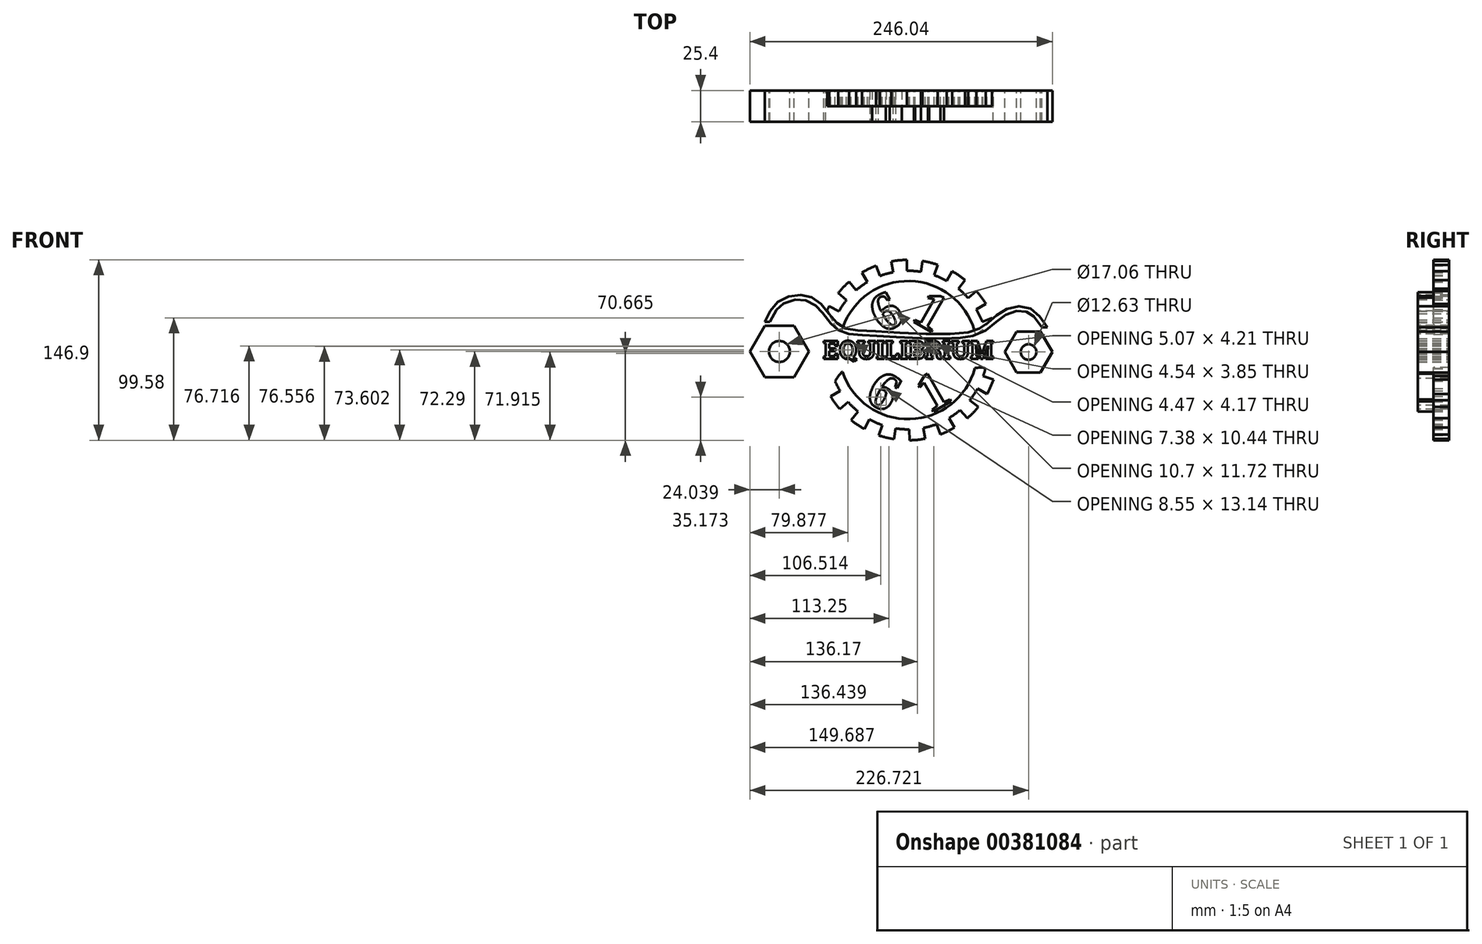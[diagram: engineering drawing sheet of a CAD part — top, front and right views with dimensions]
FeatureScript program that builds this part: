
annotation { "Feature Type Name" : "Feature", "Feature Type Description" : "" }
export const myFeature = defineFeature(function(context is Context, id is Id, definition is map)
    precondition{}
    {
        {
            var Q0;
            Q0=qCreatedBy(makeId("Front.planeOp"),FACE);
            var sketch = newSketch(context, id + "F0", { "sketchPlane" : qUnion([Q0])});
            skCircle(sketch, "E0.cCircle", {"center": v(93.86, 118.06) * mm, "radius": 16.73 * mm, "construction": true});
            skLineSegment(sketch, "E0.0", {"start": v(74.54, 118.06) * mm, "end": v(84.2, 134.79) * mm});
            skLineSegment(sketch, "E0.1", {"start": v(84.2, 134.79) * mm, "end": v(103.52, 134.79) * mm});
            skLineSegment(sketch, "E0.2", {"start": v(103.52, 134.79) * mm, "end": v(113.18, 118.06) * mm});
            skLineSegment(sketch, "E0.3", {"start": v(113.18, 118.06) * mm, "end": v(103.52, 101.32) * mm});
            skLineSegment(sketch, "E0.4", {"start": v(103.52, 101.32) * mm, "end": v(84.2, 101.32) * mm});
            skLineSegment(sketch, "E0.5", {"start": v(84.2, 101.32) * mm, "end": v(74.54, 118.06) * mm});
            skPoint(sketch, "E0.0.midPoint", {"position": v(79.37, 126.42) * mm});
            skCircle(sketch, "E1.cCircle", {"center": v(-108.82, 118.43) * mm, "radius": 20.82 * mm, "construction": true});
            skLineSegment(sketch, "E1.0", {"start": v(-84.78, 118.43) * mm, "end": v(-96.8, 97.61) * mm});
            skLineSegment(sketch, "E1.1", {"start": v(-96.8, 97.61) * mm, "end": v(-120.84, 97.61) * mm});
            skLineSegment(sketch, "E1.2", {"start": v(-120.84, 97.61) * mm, "end": v(-132.86, 118.43) * mm});
            skLineSegment(sketch, "E1.3", {"start": v(-132.86, 118.43) * mm, "end": v(-120.84, 139.25) * mm});
            skLineSegment(sketch, "E1.4", {"start": v(-120.84, 139.25) * mm, "end": v(-96.8, 139.25) * mm});
            skLineSegment(sketch, "E1.5", {"start": v(-96.8, 139.25) * mm, "end": v(-84.78, 118.43) * mm});
            skPoint(sketch, "E1.0.midPoint", {"position": v(-90.8, 108.02) * mm});
            skCircle(sketch, "E2", {"center": v(-108.82, 118.43) * mm, "radius": 8.53 * mm});
            skCircle(sketch, "E3", {"center": v(93.86, 118.06) * mm, "radius": 6.32 * mm});
            skLineSegment(sketch, "E4.0", {"start": v(82.3, 138.1) * mm, "end": v(109.3, 138.1) * mm});
            skLineSegment(sketch, "E4.1", {"start": v(70.73, 118.06) * mm, "end": v(82.3, 138.1) * mm});
            skLineSegment(sketch, "E4.2", {"start": v(82.3, 98.02) * mm, "end": v(70.73, 118.06) * mm});
            skLineSegment(sketch, "E4.3", {"start": v(103.52, 98.02) * mm, "end": v(82.3, 98.02) * mm});
            skLineSegment(sketch, "E5.0", {"start": v(-94.9, 94.3) * mm, "end": v(-120.84, 94.3) * mm});
            skLineSegment(sketch, "E5.1", {"start": v(-80.97, 118.43) * mm, "end": v(-94.9, 94.3) * mm});
            skLineSegment(sketch, "E5.2", {"start": v(-94.9, 142.55) * mm, "end": v(-80.97, 118.43) * mm});
            skLineSegment(sketch, "E5.3", {"start": v(-120.84, 142.55) * mm, "end": v(-94.9, 142.55) * mm});
            skFitSpline(sketch, "E6", {"points": [v(-120.84, 142.55) * mm, v(-109.54, 159.3) * mm, v(-89.24, 164.37) * mm, v(-74.01, 156.03) * mm, v(-59.88, 139.72) * mm, v(-39.18, 135.4) * mm, v(39.48, 133.4) * mm, v(59.02, 140.4) * mm, v(73.53, 151.68) * mm, v(93.84, 154.22) * mm, v(109.43, 137.9) * mm], "startDerivative": vector(96.51, 208.9) * mm, "endDerivative": vector(140.04, -213.02) * mm});
            skFitSpline(sketch, "E7", {"points": [v(-120.84, 94.3) * mm, v(-105.3, 79.6) * mm, v(-87.85, 76.94) * mm, v(-69.52, 87.59) * mm, v(-57.71, 99.33) * mm, v(-35.67, 104.84) * mm, v(44.99, 104.34) * mm, v(59.43, 101.49) * mm, v(73.33, 88.48) * mm, v(88.11, 84.93) * mm, v(100.24, 90.84) * mm, v(103.52, 98.02) * mm], "startDerivative": vector(157.46, -185.5) * mm, "endDerivative": vector(35.32, 133.18) * mm});
            skLineSegment(sketch, "E8.2", {"start": v(-91.96, 145.1) * mm, "end": v(-77.3, 119.7) * mm});
            skLineSegment(sketch, "E8.3", {"start": v(-77.3, 117.16) * mm, "end": v(-91.96, 91.77) * mm});
            skLineSegment(sketch, "E8.4", {"start": v(-94.16, 90.5) * mm, "end": v(-106.94, 90.5) * mm});
            skLineSegment(sketch, "E9.0", {"start": v(81.56, 141.9) * mm, "end": v(96.75, 141.9) * mm});
            skLineSegment(sketch, "E9.1", {"start": v(67.06, 119.33) * mm, "end": v(79.36, 140.63) * mm});
            skLineSegment(sketch, "E9.2", {"start": v(79.36, 95.48) * mm, "end": v(67.06, 116.79) * mm});
            skFitSpline(sketch, "E10.trimOffspring", {"points": [v(-117.38, 140.95) * mm, v(-116.38, 143.13) * mm, v(-114.9, 146.3) * mm, v(-112.76, 150.07) * mm, v(-111.3, 152.18) * mm, v(-110.04, 153.7) * mm, v(-109.04, 154.74) * mm, v(-107.98, 155.7) * mm, v(-106.85, 156.56) * mm, v(-105.6, 157.36) * mm, v(-103.8, 158.33) * mm, v(-101.36, 159.35) * mm, v(-98.2, 160.21) * mm, v(-94.98, 160.7) * mm, v(-92.36, 160.8) * mm, v(-90.37, 160.68) * mm, v(-88.96, 160.5) * mm, v(-87.6, 160.22) * mm, v(-85.89, 159.75) * mm, v(-83.86, 158.93) * mm, v(-81.54, 157.6) * mm, v(-79.66, 156.17) * mm, v(-78.17, 154.83) * mm, v(-77.07, 153.73) * mm, v(-75.96, 152.52) * mm, v(-74.84, 151.2) * mm, v(-73.71, 149.82) * mm, v(-72.2, 147.88) * mm, v(-70.27, 145.36) * mm, v(-67.9, 142.34) * mm, v(-65.8, 139.95) * mm, v(-64, 138.2) * mm, v(-62.83, 137.17) * mm, v(-61.83, 136.42) * mm, v(-60.82, 135.71) * mm, v(-59.51, 134.94) * mm, v(-57.88, 134.17) * mm, v(-55.63, 133.34) * mm, v(-52.7, 132.64) * mm, v(-48.93, 132.16) * mm, v(-45.44, 131.92) * mm, v(-42.35, 131.75) * mm, v(-39.86, 131.62) * mm, v(-37.16, 131.47) * mm, v(-33.3, 131.25) * mm, v(-28, 130.93) * mm, v(-21.08, 130.52) * mm, v(-13.73, 130.1) * mm, v(-3.57, 129.58) * mm, v(6.83, 129.15) * mm, v(16.86, 128.92) * mm, v(24.05, 128.88) * mm, v(30.77, 129) * mm, v(35.86, 129.25) * mm, v(39.58, 129.56) * mm, v(42.16, 129.85) * mm, v(44.55, 130.21) * mm, v(47.52, 130.78) * mm, v(50.84, 131.65) * mm, v(54.34, 133) * mm, v(57.44, 134.62) * mm, v(60.2, 136.47) * mm, v(62.77, 138.52) * mm, v(65.22, 140.66) * mm, v(67.64, 142.8) * mm, v(70.09, 144.84) * mm, v(72.2, 146.41) * mm, v(73.96, 147.55) * mm, v(75.32, 148.33) * mm, v(76.75, 149.05) * mm, v(78.73, 149.91) * mm, v(81.32, 150.78) * mm, v(84.47, 151.43) * mm, v(87.01, 151.6) * mm, v(88.94, 151.5) * mm, v(90.31, 151.3) * mm, v(91.4, 151.03) * mm, v(92.21, 150.76) * mm, v(93, 150.45) * mm, v(93.98, 149.97) * mm, v(95.13, 149.25) * mm, v(96.28, 148.4) * mm, v(97.8, 147.05) * mm, v(99.68, 145.06) * mm, v(101.9, 142.24) * mm, v(104.07, 139.12) * mm, v(105.51, 136.92) * mm, v(106.24, 135.81) * mm]});
            skLineSegment(sketch, "E11.trimOffspring", {"start": v(-110.44, 146.36) * mm, "end": v(-94.16, 146.36) * mm});
            skLineSegment(sketch, "E12.trimOffspring", {"start": v(90.91, 94.21) * mm, "end": v(81.56, 94.21) * mm});
            skFitSpline(sketch, "E13.0", {"points": [v(-118.32, 96.45) * mm, v(-116.68, 94.52) * mm, v(-114.27, 91.67) * mm, v(-111.02, 88.26) * mm, v(-108.57, 85.95) * mm, v(-106.49, 84.29) * mm, v(-104.8, 83.14) * mm, v(-103.52, 82.37) * mm, v(-102.22, 81.7) * mm, v(-100.44, 80.93) * mm, v(-97.24, 79.9) * mm, v(-93.44, 79.5) * mm, v(-90.04, 79.85) * mm, v(-88.1, 80.26) * mm, v(-86.12, 80.82) * mm, v(-83.62, 81.79) * mm, v(-80.63, 83.32) * mm, v(-77.72, 85.15) * mm, v(-74.94, 87.2) * mm, v(-72.78, 89.05) * mm, v(-71.17, 90.56) * mm, v(-69.63, 92.11) * mm, v(-67.77, 94.1) * mm, v(-65.6, 96.5) * mm, v(-63.37, 98.83) * mm, v(-61.38, 100.67) * mm, v(-59.64, 102.03) * mm, v(-57.8, 103.28) * mm, v(-55.34, 104.61) * mm, v(-52.03, 105.85) * mm, v(-48.33, 106.78) * mm, v(-44.13, 107.45) * mm, v(-40.1, 107.85) * mm, v(-36.5, 108.1) * mm, v(-33.59, 108.26) * mm, v(-30.47, 108.38) * mm, v(-26.08, 108.52) * mm, v(-20.2, 108.62) * mm, v(-12.66, 108.67) * mm, v(-4.8, 108.64) * mm, v(5.84, 108.53) * mm, v(19.09, 108.3) * mm, v(31.11, 108) * mm, v(39.32, 107.78) * mm, v(43.72, 107.67) * mm, v(46.7, 107.6) * mm, v(49.4, 107.52) * mm, v(51.75, 107.4) * mm, v(53.9, 107.16) * mm, v(55.46, 106.87) * mm, v(56.97, 106.46) * mm, v(58.43, 105.9) * mm, v(59.85, 105.18) * mm, v(60.98, 104.45) * mm, v(61.86, 103.8) * mm, v(62.72, 103.1) * mm, v(63.77, 102.17) * mm, v(65.01, 100.98) * mm, v(66.65, 99.31) * mm, v(68.7, 97.15) * mm, v(70.75, 95.03) * mm, v(72.4, 93.47) * mm, v(73.62, 92.4) * mm, v(74.83, 91.44) * mm, v(76.01, 90.63) * mm, v(77.22, 89.93) * mm, v(78.83, 89.15) * mm, v(80.87, 88.45) * mm, v(83.35, 88) * mm, v(85.88, 87.95) * mm, v(88.46, 88.28) * mm, v(91.07, 88.97) * mm, v(93.53, 89.97) * mm, v(95.33, 91) * mm, v(96.54, 91.87) * mm, v(97.18, 92.43) * mm, v(97.62, 92.86) * mm, v(98, 93.29) * mm, v(98.58, 94.04) * mm, v(99.2, 95.2) * mm, v(99.8, 96.87) * mm, v(100.15, 98.17) * mm, v(100.33, 98.87) * mm]});
            skPoint(sketch, "E14.visualSharp", {"position": v(-76.57, 118.43) * mm});
            skArc(sketch, "E14.filletArc", {"start": v(-77.3, 117.16) * mm, "mid": v(-76.96, 118.43) * mm, "end": v(-77.3, 119.7) * mm});
            skPoint(sketch, "E15.visualSharp", {"position": v(-92.7, 146.36) * mm});
            skArc(sketch, "E15.filletArc", {"start": v(-91.96, 145.1) * mm, "mid": v(-92.9, 146.02) * mm, "end": v(-94.16, 146.36) * mm});
            skPoint(sketch, "E16.visualSharp", {"position": v(-114.8, 146.36) * mm});
            skArc(sketch, "E16.filletArc", {"start": v(-112.58, 150.27) * mm, "mid": v(-112.67, 147.68) * mm, "end": v(-110.44, 146.36) * mm});
            skPoint(sketch, "E17.visualSharp", {"position": v(-92.7, 90.5) * mm});
            skArc(sketch, "E17.filletArc", {"start": v(-94.16, 90.5) * mm, "mid": v(-92.9, 90.84) * mm, "end": v(-91.96, 91.77) * mm});
            skArc(sketch, "E18.filletArc", {"start": v(-106.94, 90.5) * mm, "mid": v(-109.32, 88.85) * mm, "end": v(-108.61, 86.05) * mm});
            skPoint(sketch, "E19.visualSharp", {"position": v(80.1, 94.21) * mm});
            skArc(sketch, "E19.filletArc", {"start": v(79.36, 95.48) * mm, "mid": v(80.3, 94.55) * mm, "end": v(81.56, 94.21) * mm});
            skPoint(sketch, "E20.visualSharp", {"position": v(66.33, 118.06) * mm});
            skArc(sketch, "E20.filletArc", {"start": v(67.06, 119.33) * mm, "mid": v(66.72, 118.06) * mm, "end": v(67.06, 116.79) * mm});
            skPoint(sketch, "E21.visualSharp", {"position": v(80.1, 141.9) * mm});
            skArc(sketch, "E21.filletArc", {"start": v(81.56, 141.9) * mm, "mid": v(80.3, 141.56) * mm, "end": v(79.36, 140.63) * mm});
            skArc(sketch, "E22.filletArc", {"start": v(91.81, 89.3) * mm, "mid": v(93.41, 92.13) * mm, "end": v(90.91, 94.21) * mm});
            skPoint(sketch, "E23.visualSharp", {"position": v(102.1, 141.9) * mm});
            skArc(sketch, "E23.filletArc", {"start": v(96.75, 141.9) * mm, "mid": v(99.09, 143.43) * mm, "end": v(98.6, 146.18) * mm});
            skSolve(sketch);
        }
        {
            var Q0;
            Q0=qCreatedBy(makeId("Front.planeOp"),FACE);
            var sketch = newSketch(context, id + "F1", { "sketchPlane" : qUnion([Q0])});
            skText(sketch, "E24", { "text": "EQUILIBRIUM", "fontName": "RobotoSlab-Bold.ttf"});
            const initialGuessF1  = {"E24": [-0.07336, 0.11246, 1, 0, 0.01476]};
            skSetInitialGuess(sketch, initialGuessF1);
            skSolve(sketch);
        }
        {
            var Q0;
            Q0=qCreatedBy(makeId("Front.planeOp"),FACE);
            var sketch = newSketch(context, id + "F2", { "sketchPlane" : qUnion([Q0])});
            skArc(sketch, "E25", {"start": v(58.97, 157.29) * mm, "mid": v(55.45, 162.64) * mm, "end": v(51.47, 167.66) * mm});
            skLineSegment(sketch, "E26", {"start": v(-4.07, 119.59) * mm, "end": v(56.26, 142.6) * mm, "construction": true});
            skLineSegment(sketch, "E27", {"start": v(-4.07, 119.59) * mm, "end": v(-69.97, 152.06) * mm, "construction": true});
            skLineSegment(sketch, "E28", {"start": v(-4.07, 119.59) * mm, "end": v(51.34, 152.73) * mm, "construction": true});
            skLineSegment(sketch, "E29", {"start": v(-4.07, 119.59) * mm, "end": v(44.75, 161.85) * mm, "construction": true});
            skLineSegment(sketch, "E30", {"start": v(44.75, 161.85) * mm, "end": v(51.47, 167.66) * mm});
            skLineSegment(sketch, "E31", {"start": v(51.34, 152.73) * mm, "end": v(58.97, 157.29) * mm});
            skLineSegment(sketch, "E32", {"start": v(56.26, 142.6) * mm, "end": v(64.56, 145.77) * mm});
            skArc(sketch, "E33", {"start": v(56.26, 142.6) * mm, "mid": v(54.02, 147.77) * mm, "end": v(51.34, 152.73) * mm});
            skArc(sketch, "E34.1.0", {"start": v(44.75, 161.85) * mm, "mid": v(40.88, 165.94) * mm, "end": v(36.67, 169.68) * mm});
            skLineSegment(sketch, "E34.1.1", {"start": v(36.67, 169.68) * mm, "end": v(42.28, 176.58) * mm});
            skArc(sketch, "E34.1.2", {"start": v(42.28, 176.58) * mm, "mid": v(37.13, 180.4) * mm, "end": v(31.68, 183.76) * mm});
            skLineSegment(sketch, "E34.1.3", {"start": v(27.35, 176) * mm, "end": v(31.68, 183.76) * mm});
            skArc(sketch, "E34.2.0", {"start": v(27.35, 176) * mm, "mid": v(22.31, 178.52) * mm, "end": v(17.08, 180.6) * mm});
            skLineSegment(sketch, "E34.2.1", {"start": v(17.08, 180.6) * mm, "end": v(20, 189) * mm});
            skArc(sketch, "E34.2.2", {"start": v(20, 189) * mm, "mid": v(13.85, 190.83) * mm, "end": v(7.57, 192.12) * mm});
            skLineSegment(sketch, "E34.2.3", {"start": v(6.16, 183.34) * mm, "end": v(7.57, 192.12) * mm});
            skLineSegment(sketch, "E34.2.4", {"start": v(27.35, 176) * mm, "end": v(31.68, 183.76) * mm});
            skArc(sketch, "E34.3.0", {"start": v(6.16, 183.34) * mm, "mid": v(0.57, 184) * mm, "end": v(-5.06, 184.15) * mm});
            skLineSegment(sketch, "E34.3.1", {"start": v(-5.06, 184.15) * mm, "end": v(-5.2, 193.04) * mm});
            skArc(sketch, "E34.3.2", {"start": v(-5.2, 193.04) * mm, "mid": v(-11.6, 192.66) * mm, "end": v(-17.94, 191.73) * mm});
            skLineSegment(sketch, "E34.3.3", {"start": v(-16.26, 183) * mm, "end": v(-17.94, 191.73) * mm});
            skLineSegment(sketch, "E34.3.4", {"start": v(6.16, 183.34) * mm, "end": v(7.57, 192.12) * mm});
            skArc(sketch, "E34.4.0", {"start": v(-16.26, 183) * mm, "mid": v(-21.74, 181.7) * mm, "end": v(-27.09, 179.92) * mm});
            skLineSegment(sketch, "E34.4.1", {"start": v(-27.09, 179.92) * mm, "end": v(-30.25, 188.23) * mm});
            skArc(sketch, "E34.4.2", {"start": v(-30.25, 188.23) * mm, "mid": v(-36.14, 185.68) * mm, "end": v(-41.78, 182.64) * mm});
            skLineSegment(sketch, "E34.4.3", {"start": v(-37.21, 175) * mm, "end": v(-41.78, 182.64) * mm});
            skLineSegment(sketch, "E34.4.4", {"start": v(-16.26, 183) * mm, "end": v(-17.94, 191.73) * mm});
            skArc(sketch, "E34.5.0", {"start": v(-37.21, 175) * mm, "mid": v(-41.92, 171.9) * mm, "end": v(-46.33, 168.41) * mm});
            skLineSegment(sketch, "E34.5.1", {"start": v(-46.33, 168.41) * mm, "end": v(-52.15, 175.13) * mm});
            skArc(sketch, "E34.5.2", {"start": v(-52.15, 175.13) * mm, "mid": v(-56.8, 170.73) * mm, "end": v(-61.07, 165.94) * mm});
            skLineSegment(sketch, "E34.5.3", {"start": v(-54.17, 160.33) * mm, "end": v(-61.07, 165.94) * mm});
            skLineSegment(sketch, "E34.5.4", {"start": v(-37.21, 175) * mm, "end": v(-41.78, 182.64) * mm});
            skArc(sketch, "E34.6.0", {"start": v(-54.17, 160.33) * mm, "mid": v(-57.53, 155.8) * mm, "end": v(-60.48, 151.01) * mm});
            skLineSegment(sketch, "E34.6.1", {"start": v(-60.48, 151.01) * mm, "end": v(-68.25, 155.34) * mm});
            skArc(sketch, "E34.6.2", {"start": v(-68.25, 155.34) * mm, "mid": v(-71.12, 149.61) * mm, "end": v(-73.48, 143.65) * mm});
            skLineSegment(sketch, "E34.6.3", {"start": v(-65.08, 140.74) * mm, "end": v(-73.48, 143.65) * mm});
            skLineSegment(sketch, "E34.6.4", {"start": v(-54.17, 160.33) * mm, "end": v(-61.07, 165.94) * mm});
            skArc(sketch, "E34.7.0", {"start": v(-65.08, 140.74) * mm, "mid": v(-66.7, 135.34) * mm, "end": v(-67.83, 129.82) * mm});
            skLineSegment(sketch, "E34.7.1", {"start": v(-67.83, 129.82) * mm, "end": v(-76.6, 131.23) * mm});
            skArc(sketch, "E34.7.2", {"start": v(-76.6, 131.23) * mm, "mid": v(-77.35, 124.87) * mm, "end": v(-77.53, 118.46) * mm});
            skLineSegment(sketch, "E34.7.3", {"start": v(-68.64, 118.6) * mm, "end": v(-77.53, 118.46) * mm});
            skLineSegment(sketch, "E34.7.4", {"start": v(-65.08, 140.74) * mm, "end": v(-73.48, 143.65) * mm});
            skArc(sketch, "E34.8.0", {"start": v(-68.64, 118.6) * mm, "mid": v(-68.3, 112.98) * mm, "end": v(-67.49, 107.4) * mm});
            skLineSegment(sketch, "E34.8.1", {"start": v(-67.49, 107.4) * mm, "end": v(-76.22, 105.72) * mm});
            skArc(sketch, "E34.8.2", {"start": v(-76.22, 105.72) * mm, "mid": v(-74.73, 99.49) * mm, "end": v(-72.71, 93.4) * mm});
            skLineSegment(sketch, "E34.8.3", {"start": v(-64.4, 96.58) * mm, "end": v(-72.71, 93.4) * mm});
            skLineSegment(sketch, "E34.8.4", {"start": v(-68.64, 118.6) * mm, "end": v(-77.53, 118.46) * mm});
            skArc(sketch, "E34.9.0", {"start": v(-64.4, 96.58) * mm, "mid": v(-62.17, 91.4) * mm, "end": v(-59.5, 86.45) * mm});
            skLineSegment(sketch, "E34.9.1", {"start": v(-59.5, 86.45) * mm, "end": v(-67.12, 81.89) * mm});
            skArc(sketch, "E34.9.2", {"start": v(-67.12, 81.89) * mm, "mid": v(-63.6, 76.54) * mm, "end": v(-59.62, 71.51) * mm});
            skLineSegment(sketch, "E34.9.3", {"start": v(-52.9, 77.33) * mm, "end": v(-59.62, 71.51) * mm});
            skLineSegment(sketch, "E34.9.4", {"start": v(-64.4, 96.58) * mm, "end": v(-72.71, 93.4) * mm});
            skArc(sketch, "E34.10.0", {"start": v(-52.9, 77.33) * mm, "mid": v(-49.03, 73.23) * mm, "end": v(-44.82, 69.5) * mm});
            skLineSegment(sketch, "E34.10.1", {"start": v(-44.82, 69.5) * mm, "end": v(-50.43, 62.6) * mm});
            skArc(sketch, "E34.10.2", {"start": v(-50.43, 62.6) * mm, "mid": v(-45.28, 58.77) * mm, "end": v(-39.83, 55.41) * mm});
            skLineSegment(sketch, "E34.10.3", {"start": v(-35.5, 63.18) * mm, "end": v(-39.83, 55.41) * mm});
            skLineSegment(sketch, "E34.10.4", {"start": v(-52.9, 77.33) * mm, "end": v(-59.62, 71.51) * mm});
            skArc(sketch, "E34.11.0", {"start": v(-35.5, 63.18) * mm, "mid": v(-30.46, 60.66) * mm, "end": v(-25.23, 58.58) * mm});
            skLineSegment(sketch, "E34.11.1", {"start": v(-25.23, 58.58) * mm, "end": v(-28.14, 50.18) * mm});
            skArc(sketch, "E34.11.2", {"start": v(-28.14, 50.18) * mm, "mid": v(-22, 48.35) * mm, "end": v(-15.72, 47.06) * mm});
            skLineSegment(sketch, "E34.11.3", {"start": v(-14.31, 55.83) * mm, "end": v(-15.72, 47.06) * mm});
            skLineSegment(sketch, "E34.11.4", {"start": v(-35.5, 63.18) * mm, "end": v(-39.83, 55.41) * mm});
            skArc(sketch, "E34.12.0", {"start": v(-14.31, 55.83) * mm, "mid": v(-8.72, 55.18) * mm, "end": v(-3.09, 55.02) * mm});
            skLineSegment(sketch, "E34.12.1", {"start": v(-3.09, 55.02) * mm, "end": v(-2.95, 46.14) * mm});
            skArc(sketch, "E34.12.2", {"start": v(-2.95, 46.14) * mm, "mid": v(3.45, 46.51) * mm, "end": v(9.79, 47.45) * mm});
            skLineSegment(sketch, "E34.12.3", {"start": v(8.11, 56.18) * mm, "end": v(9.79, 47.45) * mm});
            skLineSegment(sketch, "E34.12.4", {"start": v(-14.31, 55.83) * mm, "end": v(-15.72, 47.06) * mm});
            skArc(sketch, "E34.13.0", {"start": v(8.11, 56.18) * mm, "mid": v(13.6, 57.48) * mm, "end": v(18.94, 59.26) * mm});
            skLineSegment(sketch, "E34.13.1", {"start": v(18.94, 59.26) * mm, "end": v(22.1, 50.95) * mm});
            skArc(sketch, "E34.13.2", {"start": v(22.1, 50.95) * mm, "mid": v(27.99, 53.5) * mm, "end": v(33.63, 56.54) * mm});
            skLineSegment(sketch, "E34.13.3", {"start": v(29.06, 64.17) * mm, "end": v(33.63, 56.54) * mm});
            skLineSegment(sketch, "E34.13.4", {"start": v(8.11, 56.18) * mm, "end": v(9.79, 47.45) * mm});
            skArc(sketch, "E34.14.0", {"start": v(29.06, 64.17) * mm, "mid": v(33.77, 67.27) * mm, "end": v(38.18, 70.77) * mm});
            skLineSegment(sketch, "E34.14.1", {"start": v(38.18, 70.77) * mm, "end": v(44, 64.04) * mm});
            skArc(sketch, "E34.14.2", {"start": v(44, 64.04) * mm, "mid": v(48.66, 68.44) * mm, "end": v(52.92, 73.24) * mm});
            skLineSegment(sketch, "E34.14.3", {"start": v(46.02, 78.84) * mm, "end": v(52.92, 73.24) * mm});
            skLineSegment(sketch, "E34.14.4", {"start": v(29.06, 64.17) * mm, "end": v(33.63, 56.54) * mm});
            skArc(sketch, "E34.15.0", {"start": v(46.02, 78.84) * mm, "mid": v(49.38, 83.37) * mm, "end": v(52.33, 88.16) * mm});
            skLineSegment(sketch, "E34.15.1", {"start": v(52.33, 88.16) * mm, "end": v(60.1, 83.84) * mm});
            skArc(sketch, "E34.15.2", {"start": v(60.1, 83.84) * mm, "mid": v(62.97, 89.57) * mm, "end": v(65.33, 95.52) * mm});
            skLineSegment(sketch, "E34.15.3", {"start": v(56.93, 98.44) * mm, "end": v(65.33, 95.52) * mm});
            skLineSegment(sketch, "E34.15.4", {"start": v(46.02, 78.84) * mm, "end": v(52.92, 73.24) * mm});
            skArc(sketch, "E34.16.0", {"start": v(56.93, 98.44) * mm, "mid": v(58.54, 103.83) * mm, "end": v(59.68, 109.35) * mm});
            skLineSegment(sketch, "E34.16.1", {"start": v(59.68, 109.35) * mm, "end": v(68.46, 107.94) * mm});
            skArc(sketch, "E34.16.2", {"start": v(68.46, 107.94) * mm, "mid": v(69.2, 114.3) * mm, "end": v(69.38, 120.71) * mm});
            skLineSegment(sketch, "E34.16.3", {"start": v(60.49, 120.58) * mm, "end": v(69.38, 120.71) * mm});
            skLineSegment(sketch, "E34.16.4", {"start": v(56.93, 98.44) * mm, "end": v(65.33, 95.52) * mm});
            skArc(sketch, "E34.17.0", {"start": v(60.49, 120.58) * mm, "mid": v(60.16, 126.2) * mm, "end": v(59.34, 131.77) * mm});
            skLineSegment(sketch, "E34.17.1", {"start": v(59.34, 131.77) * mm, "end": v(68.07, 133.45) * mm});
            skArc(sketch, "E34.17.2", {"start": v(68.07, 133.45) * mm, "mid": v(66.58, 139.69) * mm, "end": v(64.56, 145.77) * mm});
            skLineSegment(sketch, "E34.17.4", {"start": v(60.49, 120.58) * mm, "end": v(69.38, 120.71) * mm});
            skFitSpline(sketch, "E35.0", {"points": [v(-120.84, 142.55) * mm, v(-117.92, 148.88) * mm, v(-112, 161.7) * mm, v(-88.47, 166.8) * mm, v(-73.04, 157.45) * mm, v(-60.47, 136.12) * mm, v(-39.23, 135.81) * mm, v(40.04, 129.9) * mm, v(58.9, 138.9) * mm, v(72.18, 153.46) * mm, v(95.97, 158.33) * mm, v(104.94, 144.72) * mm, v(109.43, 137.9) * mm]});
            skFitSpline(sketch, "E36.0", {"points": [v(-120.84, 94.3) * mm, v(-115.97, 88.57) * mm, v(-106.72, 77.75) * mm, v(-87.25, 74.44) * mm, v(-68.7, 86.7) * mm, v(-57.98, 101.64) * mm, v(-36.08, 106.76) * mm, v(44.95, 104.21) * mm, v(59.5, 104.1) * mm, v(72.26, 86.41) * mm, v(87.82, 83.16) * mm, v(101.34, 89.77) * mm, v(102.86, 95.52) * mm, v(103.52, 98.02) * mm]});
            skCircle(sketch, "E37", {"center": v(-4.07, 119.59) * mm, "radius": 56.23 * mm});
            skSolve(sketch);
        }
        {
            var Q0;
            Q0=qCreatedBy(makeId("Front.planeOp"),FACE);
            var sketch = newSketch(context, id + "F3", { "sketchPlane" : qUnion([Q0])});
            skText(sketch, "E38", { "text": "6", "fontName": "Tinos-Bold.ttf"});
            skPoint(sketch, "E39.0", {"position": v(-3.5, 119.84) * mm});
            skLineSegment(sketch, "E40", {"start": v(-3.5, 119.84) * mm, "end": v(-40.45, 183.81) * mm, "construction": true});
            skLineSegment(sketch, "E41", {"start": v(-3.5, 119.84) * mm, "end": v(33.01, 183.1) * mm, "construction": true});
            skText(sketch, "E42", { "text": "1", "fontName": "Tinos-Bold.ttf"});
            skLineSegment(sketch, "E43", {"start": v(-3.5, 119.84) * mm, "end": v(-3.5, 138.31) * mm, "construction": true});
            skLineSegment(sketch, "E44", {"start": v(-3.5, 119.84) * mm, "end": v(-30.78, 72.6) * mm, "construction": true});
            skLineSegment(sketch, "E45", {"start": v(-3.5, 119.84) * mm, "end": v(24.5, 71.33) * mm, "construction": true});
            skText(sketch, "E46", { "text": "1", "fontName": "Tinos-Bold.ttf"});
            skText(sketch, "E47", { "text": "6", "fontName": "Tinos-Bold.ttf"});
            skCircle(sketch, "E48", {"center": v(-3.5, 119.84) * mm, "radius": 21.76 * mm, "construction": true});
            const initialGuessF3  = {"E38": [-0.02457, 0.1328, 0.86603, 0.5, 0.03175], "E42": [-0.00238, 0.14431, 0.86603, -0.5, 0.03175], "E46": [0.0135, 0.06786, 0.86603, 0.5, 0.03175], "E47": [-0.04045, 0.07937, 0.86603, -0.5, 0.03175]};
            skSetInitialGuess(sketch, initialGuessF3);
            skSolve(sketch);
        }
        {
            var Q0;
            Q0=makeQuery(id+"F2.imprint","IMPRINT",FACE,{"disambiguationData":[TD([[makeQuery(id+"F2.imprint","IMPRINT",EDGE,{"derivedFrom":sQuery(id+"F2.wireOp",EDGE,"E25")}),1.0]])]});
            var Q1;
            {var subQ0=sQuery(id+"F2.wireOp",EDGE,"E34.9.1");Q1=makeQuery(id+"F2.imprint","IMPRINT",FACE,{"disambiguationData":[TD([[makeQuery(id+"F2.imprint","IMPRINT",EDGE,{"derivedFrom":subQ0}),1.0]])]});}
            extrude(context, id + "F4", {"entities" : qUnion([Q0, Q1]), "depth" : 12.7 * mm});
        }
        {
            var Q0;
            {var subQ0=sQuery(id+"F0.wireOp",EDGE,"E4.0");Q0=makeQuery(id+"F0.imprint","IMPRINT",FACE,{"disambiguationData":[TD([[makeQuery(id+"F0.imprint","IMPRINT",EDGE,{"derivedFrom":subQ0}),1.0]])]});}
            var Q1;
            Q1=makeQuery(id+"F0.imprint","IMPRINT",FACE,{"disambiguationData":[TD([[makeQuery(id+"F0.imprint","IMPRINT",EDGE,{"derivedFrom":sQuery(id+"F0.wireOp",EDGE,"E1.0")}),-1.0]])]});
            var Q2;
            Q2=makeQuery(id+"F0.imprint","IMPRINT",FACE,{"disambiguationData":[TD([[makeQuery(id+"F0.imprint","IMPRINT",EDGE,{"derivedFrom":sQuery(id+"F0.wireOp",EDGE,"E0.0")}),-1.0]])]});
            var Q3;
            Q3=qSketchRegion(id+"F1",true);
            var Q4;
            Q4=qSketchRegion(id+"F3",true);
            extrude(context, id + "F5", {"entities" : qUnion([Q0, Q1, Q2, Q3, Q4]), "depth" : 25.4 * mm});
        }
    });
